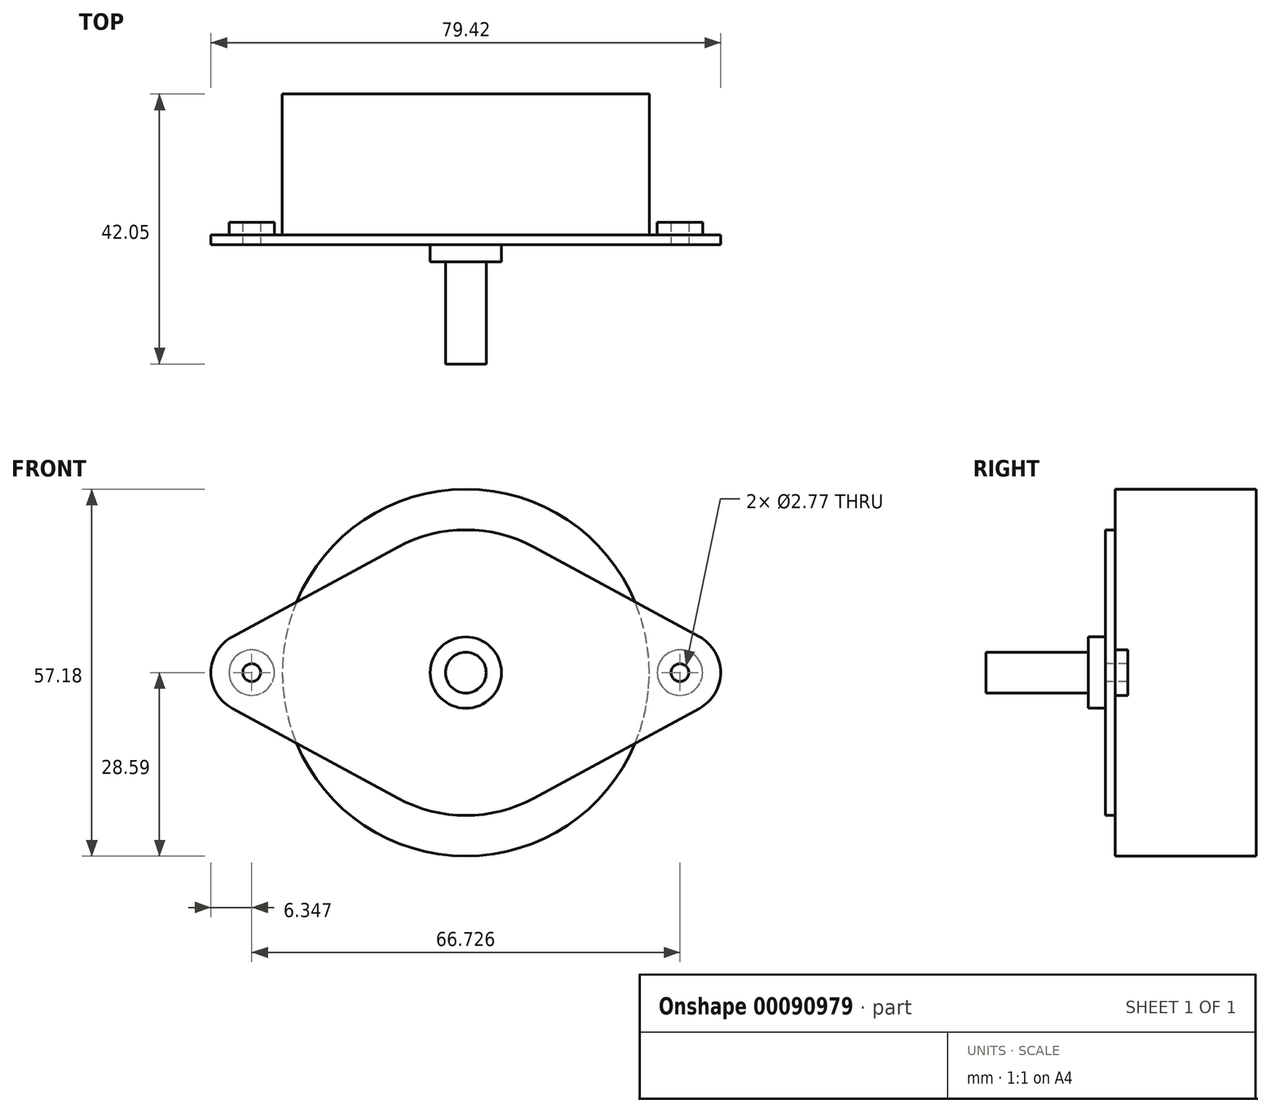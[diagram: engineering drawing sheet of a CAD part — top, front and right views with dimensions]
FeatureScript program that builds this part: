
annotation { "Feature Type Name" : "Feature", "Feature Type Description" : "" }
export const myFeature = defineFeature(function(context is Context, id is Id, definition is map)
    precondition{}
    {
        {
            var Q0;
            Q0=qCreatedBy(makeId("Front.planeOp"),FACE);
            var sketch = newSketch(context, id + "F0", { "sketchPlane" : qUnion([Q0])});
            skCircle(sketch, "E0", {"center": v(0, 0) * mm, "radius": 28.59 * mm});
            skSolve(sketch);
        }
        {
            var Q0;
            Q0 = qSketchRegion(id + "F0", true);
            extrude(context, id + "F1", {"entities" : qUnion([Q0]), "oppositeDirection" : true, "depth" : 21.93 * mm});
        }
        {
            var Q0;
            Q0=makeQuery(id+"F1.opExtrude","CAP_FACE",FACE,{"disambiguationData":[OSD([sQuery(id+"F0.wireOp",EDGE,"E0")])],"isStart":true});
            var sketch = newSketch(context, id + "F2", { "sketchPlane" : qUnion([Q0])});
            skCircle(sketch, "E1", {"center": v(0, 0) * mm, "radius": 22.25 * mm, "construction": true});
            skCircle(sketch, "E2", {"center": v(-33.36, 0) * mm, "radius": 6.35 * mm, "construction": true});
            skCircle(sketch, "E3", {"center": v(33.36, 0) * mm, "radius": 6.35 * mm, "construction": true});
            skLineSegment(sketch, "E4", {"start": v(-36.39, 5.58) * mm, "end": v(-10.6, 19.56) * mm});
            skLineSegment(sketch, "E5", {"start": v(10.6, 19.56) * mm, "end": v(36.39, 5.58) * mm});
            skLineSegment(sketch, "E6", {"start": v(36.39, -5.58) * mm, "end": v(10.6, -19.56) * mm});
            skLineSegment(sketch, "E7", {"start": v(-10.6, -19.56) * mm, "end": v(-36.39, -5.58) * mm});
            skArc(sketch, "E8", {"start": v(-10.6, 19.56) * mm, "mid": v(0, 22.25) * mm, "end": v(10.6, 19.56) * mm});
            skArc(sketch, "E9", {"start": v(10.6, -19.56) * mm, "mid": v(0, -22.25) * mm, "end": v(-10.6, -19.56) * mm});
            skArc(sketch, "E10", {"start": v(-36.39, 5.58) * mm, "mid": v(-39.71, 0) * mm, "end": v(-36.39, -5.58) * mm});
            skArc(sketch, "E11", {"start": v(36.39, 5.58) * mm, "mid": v(39.71, 0) * mm, "end": v(36.39, -5.58) * mm});
            skLineSegment(sketch, "E12", {"start": v(-33.36, 0) * mm, "end": v(0, 0) * mm, "construction": true});
            skLineSegment(sketch, "E13", {"start": v(0, 0) * mm, "end": v(33.36, 0) * mm, "construction": true});
            skSolve(sketch);
        }
        {
            var Q0;
            Q0 = qSketchRegion(id + "F2", true);
            extrude(context, id + "F3", {"entities" : qUnion([Q0]), "operationType" : NewBodyOperationType.ADD, "depth" : 1.54 * mm});
        }
        {
            var Q0;
            Q0=makeQuery(id+"F3.opExtrude","CAP_FACE",FACE,{"disambiguationData":[OSD([sQuery(id+"F2.wireOp",EDGE,"E4"),sQuery(id+"F2.wireOp",EDGE,"E5"),sQuery(id+"F2.wireOp",EDGE,"E6"),sQuery(id+"F2.wireOp",EDGE,"E7"),sQuery(id+"F2.wireOp",EDGE,"E8"),sQuery(id+"F2.wireOp",EDGE,"E9"),sQuery(id+"F2.wireOp",EDGE,"E10"),sQuery(id+"F2.wireOp",EDGE,"E11")])],"isStart":false});
            var sketch = newSketch(context, id + "F4", { "sketchPlane" : qUnion([Q0])});
            skCircle(sketch, "E14", {"center": v(0, 0) * mm, "radius": 5.56 * mm});
            skSolve(sketch);
        }
        {
            var Q0;
            Q0 = qSketchRegion(id + "F4", true);
            extrude(context, id + "F5", {"entities" : qUnion([Q0]), "operationType" : NewBodyOperationType.ADD, "depth" : 2.7 * mm});
        }
        {
            var Q0;
            Q0=makeQuery(id+"F5.opExtrude","CAP_FACE",FACE,{"disambiguationData":[OSD([sQuery(id+"F4.wireOp",EDGE,"E14")])],"isStart":false});
            var sketch = newSketch(context, id + "F6", { "sketchPlane" : qUnion([Q0])});
            skCircle(sketch, "E15", {"center": v(0, 0) * mm, "radius": 3.18 * mm});
            skSolve(sketch);
        }
        {
            var Q0;
            Q0 = qSketchRegion(id + "F6", true);
            extrude(context, id + "F7", {"entities" : qUnion([Q0]), "operationType" : NewBodyOperationType.ADD, "depth" : 15.9 * mm});
        }
        {
            var Q0;
            {var subQ0=sQuery(id+"F2.wireOp",EDGE,"E7");var subQ2=sQuery(id+"F2.wireOp",EDGE,"E4");var subQ3=sQuery(id+"F2.wireOp",EDGE,"E10");Q0=makeQuery(id+"F3.boolean.opBoolean","SPLIT",FACE,{"disambiguationData":[TD([makeQuery(id+"F3.opExtrude","SWEPT_FACE",FACE,{"disambiguationData":[OSD([subQ2])]})])],"derivedFrom":makeQuery(id+"F3.opExtrude","CAP_FACE",FACE,{"disambiguationData":[OSD([subQ2,sQuery(id+"F2.wireOp",EDGE,"E5"),sQuery(id+"F2.wireOp",EDGE,"E6"),subQ0,sQuery(id+"F2.wireOp",EDGE,"E8"),sQuery(id+"F2.wireOp",EDGE,"E9"),subQ3,sQuery(id+"F2.wireOp",EDGE,"E11")])],"isStart":true})});}
            var sketch = newSketch(context, id + "F8", { "sketchPlane" : qUnion([Q0])});
            skCircle(sketch, "E16", {"center": v(33.36, 0) * mm, "radius": 3.54 * mm});
            skCircle(sketch, "E17", {"center": v(-33.36, 0) * mm, "radius": 3.54 * mm});
            skSolve(sketch);
        }
        {
            var Q0;
            Q0=makeQuery(id+"F8.imprint","IMPRINT",FACE,{"disambiguationData":[TD([[makeQuery(id+"F8.imprint","IMPRINT",EDGE,{"derivedFrom":sQuery(id+"F8.wireOp",EDGE,"E17")}),1.0]])]});
            var Q1;
            Q1=makeQuery(id+"F8.imprint","IMPRINT",FACE,{"disambiguationData":[TD([[makeQuery(id+"F8.imprint","IMPRINT",EDGE,{"derivedFrom":sQuery(id+"F8.wireOp",EDGE,"E16")}),1.0]])]});
            extrude(context, id + "F9", {"entities" : qUnion([Q0, Q1]), "operationType" : NewBodyOperationType.ADD, "depth" : 1.98 * mm});
        }
        {
            var Q0;
            Q0=makeQuery(id+"F3.opExtrude","CAP_FACE",FACE,{"disambiguationData":[OSD([sQuery(id+"F2.wireOp",EDGE,"E4"),sQuery(id+"F2.wireOp",EDGE,"E5"),sQuery(id+"F2.wireOp",EDGE,"E6"),sQuery(id+"F2.wireOp",EDGE,"E7"),sQuery(id+"F2.wireOp",EDGE,"E8"),sQuery(id+"F2.wireOp",EDGE,"E9"),sQuery(id+"F2.wireOp",EDGE,"E10"),sQuery(id+"F2.wireOp",EDGE,"E11")])],"isStart":false});
            var sketch = newSketch(context, id + "F10", { "sketchPlane" : qUnion([Q0])});
            skCircle(sketch, "E18", {"center": v(33.36, 0) * mm, "radius": 1.38 * mm});
            skCircle(sketch, "E19", {"center": v(-33.36, 0) * mm, "radius": 1.38 * mm});
            skSolve(sketch);
        }
        {
            var Q0;
            Q0 = qSketchRegion(id + "F10", true);
            extrude(context, id + "F11", {"entities" : qUnion([Q0]), "operationType" : NewBodyOperationType.REMOVE, "endBound" : BoundingType.THROUGH_ALL, "oppositeDirection" : true, "depth" : 25.4 * mm});
        }
    });
